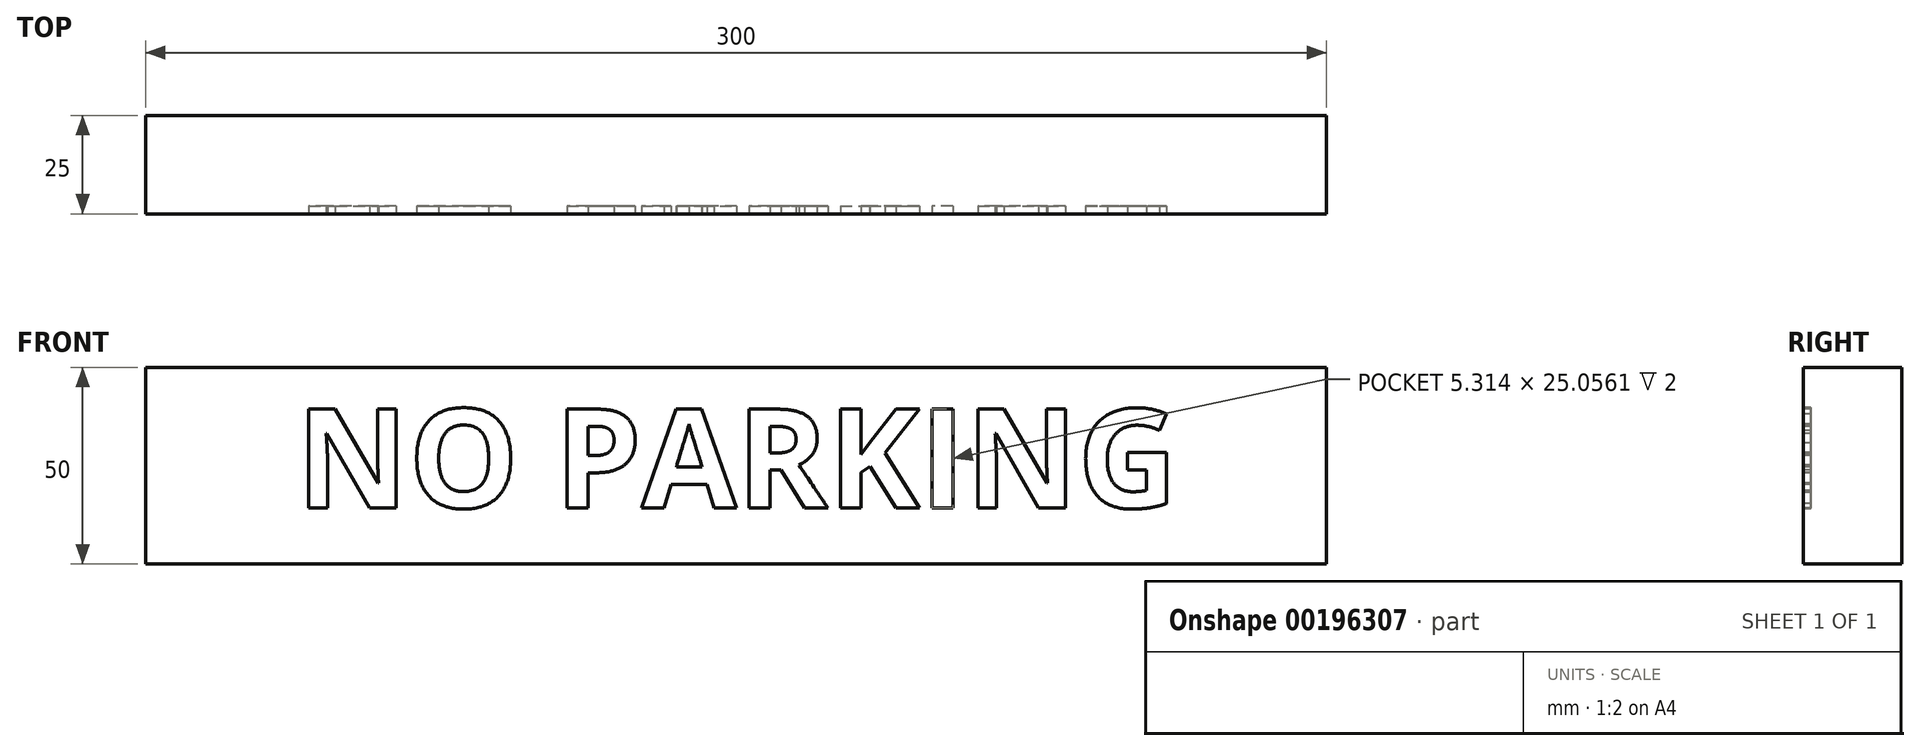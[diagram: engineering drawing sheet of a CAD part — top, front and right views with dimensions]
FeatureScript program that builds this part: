
annotation { "Feature Type Name" : "Feature", "Feature Type Description" : "" }
export const myFeature = defineFeature(function(context is Context, id is Id, definition is map)
    precondition{}
    {
        {
            var Q0;
            Q0=qCreatedBy(makeId("Front.planeOp"),FACE);
            var sketch = newSketch(context, id + "F0", { "sketchPlane" : qUnion([Q0])});
            skLineSegment(sketch, "E0.bottom", {"start": v(-150, 25) * mm, "end": v(150, 25) * mm});
            skLineSegment(sketch, "E0.top", {"start": v(-150, -25) * mm, "end": v(150, -25) * mm});
            skLineSegment(sketch, "E0.left", {"start": v(-150, 25) * mm, "end": v(-150, -25) * mm});
            skLineSegment(sketch, "E0.right", {"start": v(150, 25) * mm, "end": v(150, -25) * mm});
            skPoint(sketch, "E0.middle", {"position": v(0, 0) * mm});
            skSolve(sketch);
        }
        {
            var Q0;
            Q0 = qSketchRegion(id + "F0", true);
            extrude(context, id + "F1", {"entities" : qUnion([Q0]), "depth" : 25 * mm});
        }
        {
            var Q0;
            Q0=makeQuery(id+"F1.opExtrude","CAP_FACE",FACE,{"disambiguationData":[OSD([sQuery(id+"F0.wireOp",EDGE,"E0.bottom"),sQuery(id+"F0.wireOp",EDGE,"E0.top"),sQuery(id+"F0.wireOp",EDGE,"E0.left"),sQuery(id+"F0.wireOp",EDGE,"E0.right")])],"isStart":false});
            var sketch = newSketch(context, id + "F2", { "sketchPlane" : qUnion([Q0])});
            skText(sketch, "E1", { "text": "NO PARKING", "fontName": "OpenSans-Bold.ttf"});
            const initialGuessF2  = {"E1": [-0.11167, -0.0107, 1, 0, 0.02527]};
            skSetInitialGuess(sketch, initialGuessF2);
            skSolve(sketch);
        }
        {
            var Q0;
            Q0 = qSketchRegion(id + "F2", true);
            extrude(context, id + "F3", {"entities" : qUnion([Q0]), "operationType" : NewBodyOperationType.REMOVE, "oppositeDirection" : true, "depth" : 2 * mm});
        }
    });
